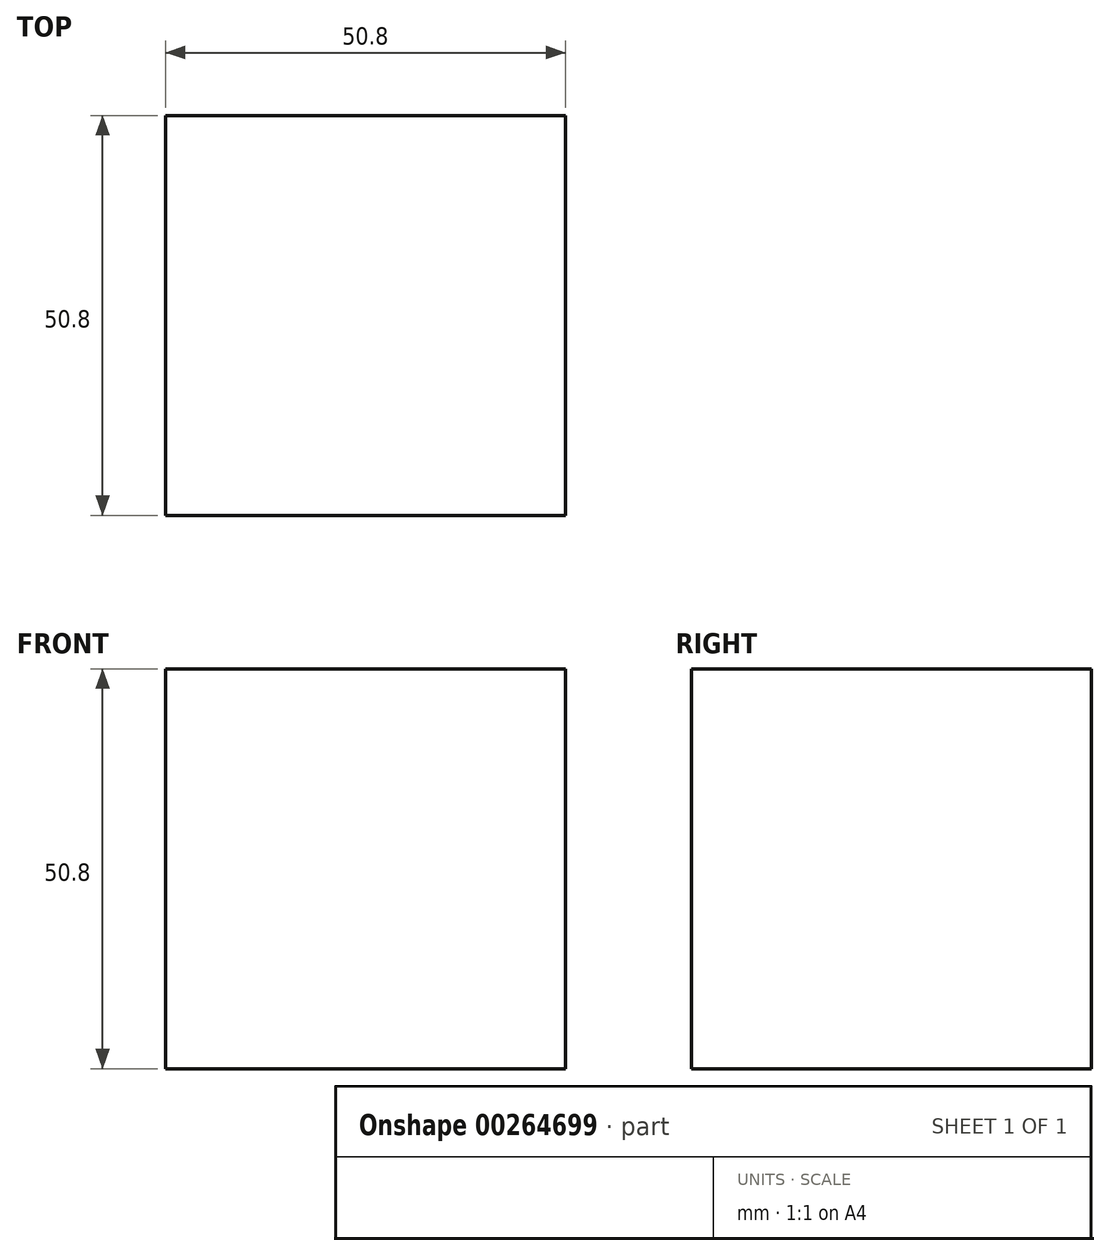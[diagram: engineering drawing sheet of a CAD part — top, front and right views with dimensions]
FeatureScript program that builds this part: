
annotation { "Feature Type Name" : "Feature", "Feature Type Description" : "" }
export const myFeature = defineFeature(function(context is Context, id is Id, definition is map)
    precondition{}
    {
        {
            var Q0;
            Q0=qCreatedBy(makeId("Front.planeOp"),FACE);
            var sketch = newSketch(context, id + "F0", { "sketchPlane" : qUnion([Q0])});
            skLineSegment(sketch, "E0.bottom", {"start": v(25.4, 25.4) * mm, "end": v(-25.4, 25.4) * mm});
            skLineSegment(sketch, "E0.top", {"start": v(25.4, -25.4) * mm, "end": v(-25.4, -25.4) * mm});
            skLineSegment(sketch, "E0.left", {"start": v(25.4, 25.4) * mm, "end": v(25.4, -25.4) * mm});
            skLineSegment(sketch, "E0.right", {"start": v(-25.4, 25.4) * mm, "end": v(-25.4, -25.4) * mm});
            skPoint(sketch, "E0.middle", {"position": v(0, 0) * mm});
            skSolve(sketch);
        }
        {
            var Q0;
            Q0=makeQuery(id+"F0.imprint","IMPRINT",FACE,{"disambiguationData":[TD([[makeQuery(id+"F0.imprint","IMPRINT",EDGE,{"derivedFrom":sQuery(id+"F0.wireOp",EDGE,"E0.bottom")}),1.0]])]});
            extrude(context, id + "F1", {"entities" : qUnion([Q0]), "depth" : 50.8 * mm});
        }
    });
